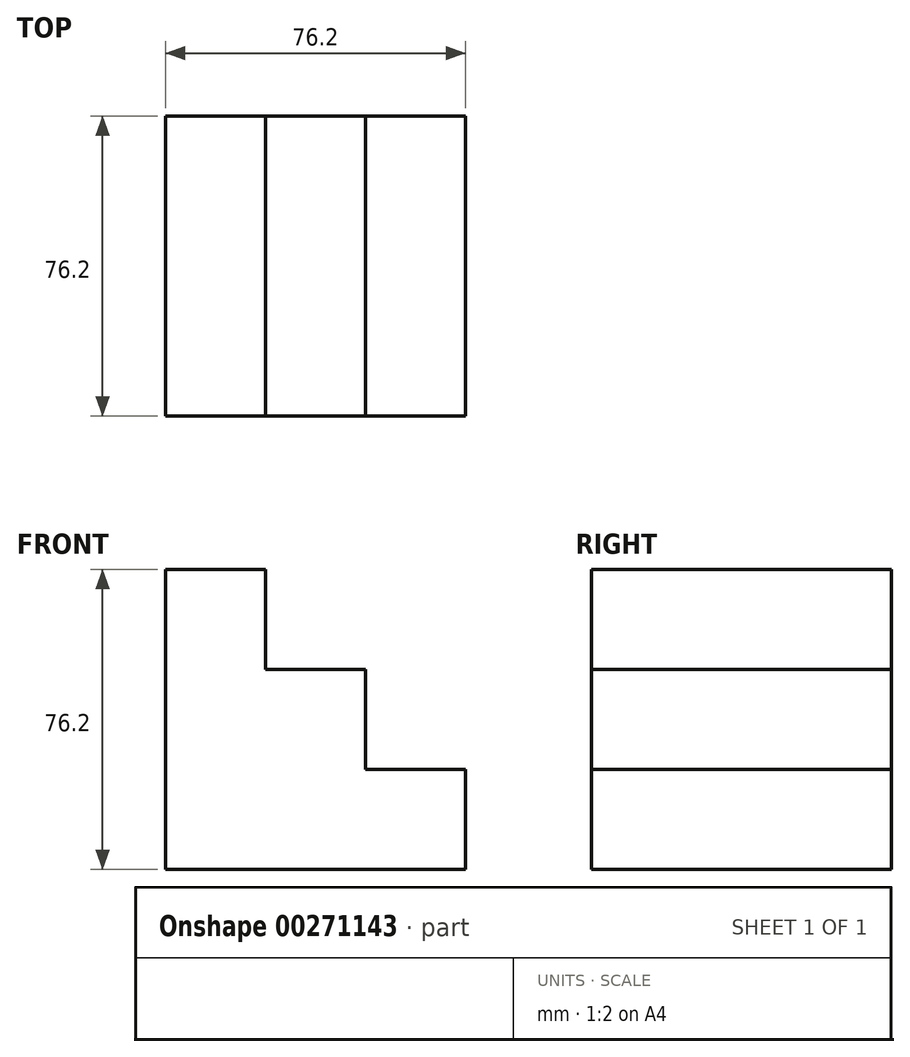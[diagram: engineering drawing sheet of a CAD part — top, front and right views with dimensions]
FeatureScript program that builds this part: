
annotation { "Feature Type Name" : "Feature", "Feature Type Description" : "" }
export const myFeature = defineFeature(function(context is Context, id is Id, definition is map)
    precondition{}
    {
        {
            var Q0;
            Q0=qCreatedBy(makeId("Front.planeOp"),FACE);
            var sketch = newSketch(context, id + "F0", { "sketchPlane" : qUnion([Q0])});
            skLineSegment(sketch, "E0", {"start": v(-50.03, -71.42) * mm, "end": v(-50.03, 4.78) * mm});
            skLineSegment(sketch, "E1", {"start": v(-50.03, 4.78) * mm, "end": v(-24.63, 4.78) * mm});
            skLineSegment(sketch, "E2", {"start": v(-24.63, 4.78) * mm, "end": v(-24.63, -20.62) * mm});
            skLineSegment(sketch, "E3", {"start": v(-24.63, -20.62) * mm, "end": v(0.77, -20.62) * mm});
            skLineSegment(sketch, "E4", {"start": v(0.77, -20.62) * mm, "end": v(0.77, -46.02) * mm});
            skLineSegment(sketch, "E5", {"start": v(0.77, -46.02) * mm, "end": v(26.17, -46.02) * mm});
            skLineSegment(sketch, "E6", {"start": v(26.17, -46.02) * mm, "end": v(26.17, -71.42) * mm});
            skLineSegment(sketch, "E7", {"start": v(26.17, -71.42) * mm, "end": v(-50.03, -71.42) * mm});
            skSolve(sketch);
        }
        {
            var Q0;
            Q0 = qSketchRegion(id + "F0", true);
            extrude(context, id + "F1", {"entities" : qUnion([Q0]), "depth" : 76.2 * mm});
        }
    });
